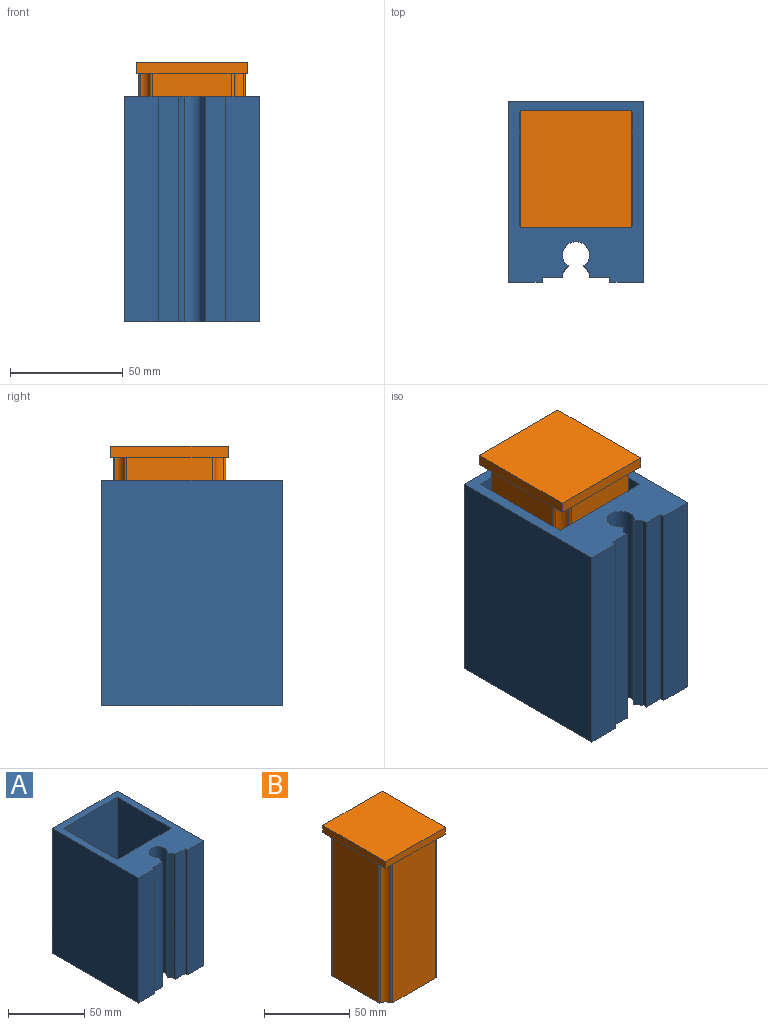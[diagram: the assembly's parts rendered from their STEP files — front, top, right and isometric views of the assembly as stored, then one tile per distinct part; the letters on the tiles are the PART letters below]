
ASSEMBLY  parts=2 mates=2
PART A: 21 faces, bbox 60x80x100 mm
  f0: plane 80x60mm, normal (0,0,1), area 2078.6mm2, adj f1,f2,f3,f4,f5,f6,f7,f8
  f1: plane 100x80mm, normal (-1,0,0), area 8000mm2, adj f0,f2,f14,f15
  f2: plane 100x15mm, normal (0,-1,0), area 1500mm2, adj f0,f1,f3,f15
  f3: plane 100x2mm, normal (1,0,0), area 200mm2, adj f0,f2,f4,f15
  f4: plane 100x9mm, normal (0,-1,0), area 900mm2, adj f0,f3,f5,f15
  f5: plane 100x2mm, normal (1,0,0), area 200mm2, adj f0,f4,f6,f15
  f6: plane 100x3.13mm, normal (0.78,-0.62,0), area 400.3mm2, adj f0,f5,f7,f15
  f7: cylinder r=6mm len=100mm, axis (0,0,-1), area 3022.5mm2, adj f0,f6,f8,f15
  f8: plane 100x3.13mm, normal (-0.78,-0.62,0), area 400.3mm2, adj f0,f7,f9,f15
  f9: plane 100x2mm, normal (-1,0,0), area 200mm2, adj f0,f8,f10,f15
  f10: plane 100x9mm, normal (0,-1,0), area 900mm2, adj f0,f9,f11,f15
  f11: plane 100x2mm, normal (-1,0,0), area 200mm2, adj f0,f10,f12,f15
  f12: plane 100x15mm, normal (0,-1,0), area 1500mm2, adj f0,f11,f13,f15
  f13: plane 100x80mm, normal (1,0,0), area 8000mm2, adj f0,f12,f14,f15
  f14: plane 100x60mm, normal (0,1,0), area 6000mm2, adj f0,f1,f13,f15
  f15: plane 80x60mm, normal (0,0,-1), area 4578.6mm2, adj f1,f2,f3,f4,f5,f6,f7,f8
  f16: plane 90x50mm, normal (0,-1,0), area 4500mm2, adj f0,f17,f19,f20
  f17: plane 90x50mm, normal (1,0,0), area 4500mm2, adj f0,f16,f18,f20
  f18: plane 90x50mm, normal (0,1,0), area 4500mm2, adj f0,f17,f19,f20
  f19: plane 90x50mm, normal (-1,0,0), area 4500mm2, adj f0,f16,f18,f20
  f20: plane 50x50mm, normal (0,0,1), area 2500mm2, adj f16,f17,f18,f19
PART B: 23 faces, bbox 49.3x52x105 mm
  f0: cylinder r=5mm len=100mm, axis (0,0,-1), area 618mm2, adj f1,f15,f16,f17
  f1: cylinder r=1mm len=100mm, axis (0,0,-1), area 140.3mm2, adj f0,f2,f16,f17
  f2: plane 100x35.42mm, normal (0,-1,0), area 3542.4mm2, adj f1,f3,f16,f17
  f3: cylinder r=1mm len=100mm, axis (0,0,-1), area 140.3mm2, adj f2,f4,f16,f17
  f4: cylinder r=5mm len=100mm, axis (0,0,-1), area 617.9mm2, adj f3,f5,f16,f17
  f5: cylinder r=1mm len=100mm, axis (0,0,-1), area 140.3mm2, adj f4,f6,f16,f17
  f6: plane 100x38.17mm, normal (1,0,0), area 3816.8mm2, adj f5,f7,f16,f17
  f7: cylinder r=1mm len=100mm, axis (0,0,-1), area 140.3mm2, adj f6,f8,f16,f17
  f8: cylinder r=5mm len=100mm, axis (0,0,-1), area 618mm2, adj f7,f9,f16,f17
  f9: cylinder r=1mm len=100mm, axis (0,0,-1), area 140.3mm2, adj f8,f10,f16,f17
  f10: plane 100x35.42mm, normal (0,1,0), area 3542.4mm2, adj f9,f11,f16,f17
  f11: cylinder r=1mm len=100mm, axis (0,0,-1), area 140.3mm2, adj f10,f12,f16,f17
  f12: cylinder r=5mm len=100mm, axis (0,0,-1), area 618mm2, adj f11,f13,f16,f17
  f13: cylinder r=1mm len=100mm, axis (0,0,-1), area 140.3mm2, adj f12,f14,f16,f17
  f14: plane 100x38.17mm, normal (-1,0,0), area 3816.8mm2, adj f13,f15,f16,f17
  f15: cylinder r=1mm len=100mm, axis (0,0,-1), area 140.3mm2, adj f0,f14,f16,f17
  f16: plane 50x47.26mm, normal (0,0,-1), area 2282.9mm2, adj f0,f1,f2,f3,f4,f5,f6,f7
  f17: plane 52x49.26mm, normal (0,0,-1), area 278.4mm2, adj f0,f1,f2,f3,f4,f5,f6,f7
  f18: plane 49.26x5mm, normal (0,1,0), area 246.3mm2, adj f17,f19,f21,f22
  f19: plane 52x5mm, normal (-1,0,0), area 260mm2, adj f17,f18,f20,f22
  f20: plane 49.26x5mm, normal (0,-1,0), area 246.3mm2, adj f17,f19,f21,f22
  f21: plane 52x5mm, normal (1,0,0), area 260mm2, adj f17,f18,f20,f22
  f22: plane 52x49.26mm, normal (0,0,1), area 2561.3mm2, adj f18,f19,f20,f21
PLACE A t=(-30,-30,-10)mm
PLACE B t=(68.52,-35.18,0)mm
MATE planar B.f16 <-> A.f20  axis (0,0,-1) through (0,0,0)mm
MATE fastened B.f16 <-> A.f20  axis (0,0,-1) through (0,0,0)mm
